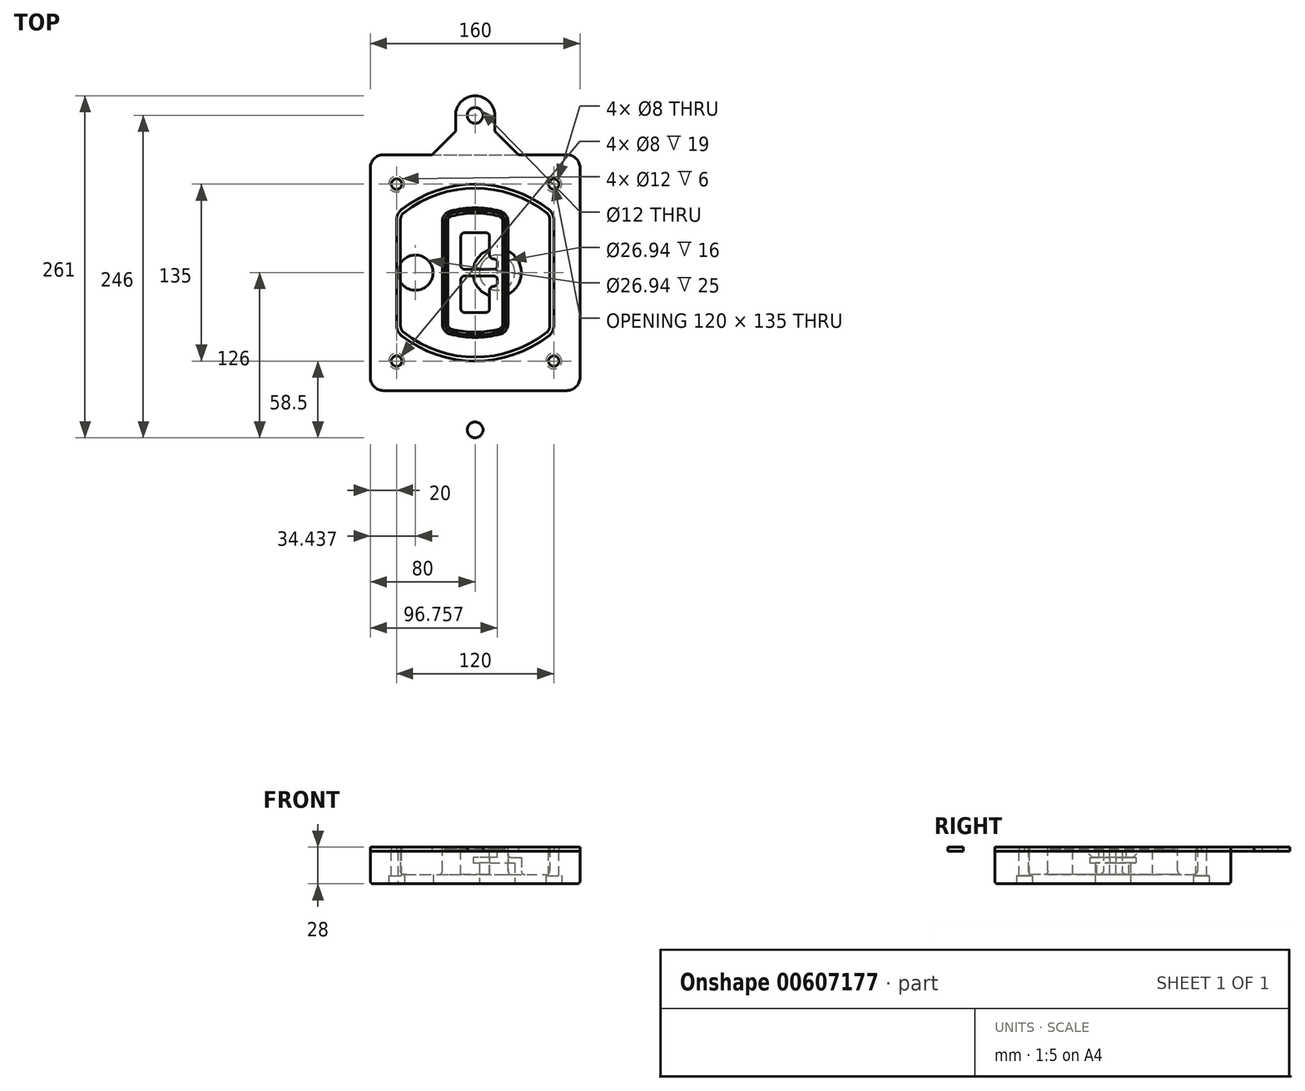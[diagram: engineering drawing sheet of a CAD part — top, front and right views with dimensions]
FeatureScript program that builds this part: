
annotation { "Feature Type Name" : "Feature", "Feature Type Description" : "" }
export const myFeature = defineFeature(function(context is Context, id is Id, definition is map)
    precondition{}
    {
        {
            var Q0;
            Q0=qCreatedBy(makeId("Top.planeOp"),FACE);
            var sketch = newSketch(context, id + "F0", { "sketchPlane" : qUnion([Q0])});
            skPoint(sketch, "E0.rect.middle", {"position": v(0, 0) * mm});
            skLineSegment(sketch, "E1.bottom", {"start": v(-70, -90) * mm, "end": v(70, -90) * mm});
            skLineSegment(sketch, "E1.top", {"start": v(-70, 90) * mm, "end": v(70, 90) * mm});
            skLineSegment(sketch, "E1.left", {"start": v(-80, -80) * mm, "end": v(-80, 80) * mm});
            skLineSegment(sketch, "E1.right", {"start": v(80, -80) * mm, "end": v(80, 80) * mm});
            skLineSegment(sketch, "E2", {"start": v(-80, 90) * mm, "end": v(80, -90) * mm, "construction": true});
            skLineSegment(sketch, "E3", {"start": v(80, 90) * mm, "end": v(-80, -90) * mm, "construction": true});
            skCircle(sketch, "E4", {"center": v(-60, 67.5) * mm, "radius": 4 * mm});
            skCircle(sketch, "E5", {"center": v(60, 67.5) * mm, "radius": 4 * mm});
            skCircle(sketch, "E6", {"center": v(60, -67.5) * mm, "radius": 4 * mm});
            skCircle(sketch, "E7", {"center": v(-60, -67.5) * mm, "radius": 4 * mm});
            skLineSegment(sketch, "E8", {"start": v(-60, 67.5) * mm, "end": v(60, 67.5) * mm, "construction": true});
            skLineSegment(sketch, "E9", {"start": v(60, 67.5) * mm, "end": v(60, -67.5) * mm, "construction": true});
            skLineSegment(sketch, "E10", {"start": v(60, -67.5) * mm, "end": v(-60, -67.5) * mm, "construction": true});
            skLineSegment(sketch, "E11", {"start": v(-60, -67.5) * mm, "end": v(-60, 67.5) * mm, "construction": true});
            skLineSegment(sketch, "E12", {"start": v(-60, 40.3) * mm, "end": v(-60, -40.3) * mm});
            skLineSegment(sketch, "E13", {"start": v(60, 40.3) * mm, "end": v(60, -40.3) * mm});
            skArc(sketch, "E14", {"start": v(56.15, 48.18) * mm, "mid": v(0, 67.5) * mm, "end": v(-56.15, 48.18) * mm});
            skArc(sketch, "E15", {"start": v(-56.15, -48.18) * mm, "mid": v(0, -67.5) * mm, "end": v(56.15, -48.18) * mm});
            skLineSegment(sketch, "E16", {"start": v(-60, 0) * mm, "end": v(60, 0) * mm, "construction": true});
            skPoint(sketch, "E17.visualSharp", {"position": v(-60, -45) * mm});
            skArc(sketch, "E17.filletArc", {"start": v(-60, -40.3) * mm, "mid": v(-58.99, -44.68) * mm, "end": v(-56.15, -48.18) * mm});
            skPoint(sketch, "E18.visualSharp", {"position": v(-60, 45) * mm});
            skArc(sketch, "E18.filletArc", {"start": v(-56.15, 48.18) * mm, "mid": v(-58.99, 44.68) * mm, "end": v(-60, 40.3) * mm});
            skPoint(sketch, "E19.visualSharp", {"position": v(60, 45) * mm});
            skArc(sketch, "E19.filletArc", {"start": v(60, 40.3) * mm, "mid": v(58.99, 44.68) * mm, "end": v(56.15, 48.18) * mm});
            skPoint(sketch, "E20.visualSharp", {"position": v(60, -45) * mm});
            skArc(sketch, "E20.filletArc", {"start": v(56.15, -48.18) * mm, "mid": v(58.99, -44.68) * mm, "end": v(60, -40.3) * mm});
            skPoint(sketch, "E21.visualSharp", {"position": v(-80, 90) * mm});
            skArc(sketch, "E21.filletArc", {"start": v(-70, 90) * mm, "mid": v(-77.07, 87.07) * mm, "end": v(-80, 80) * mm});
            skPoint(sketch, "E22.visualSharp", {"position": v(80, 90) * mm});
            skArc(sketch, "E22.filletArc", {"start": v(80, 80) * mm, "mid": v(77.07, 87.07) * mm, "end": v(70, 90) * mm});
            skPoint(sketch, "E23.visualSharp", {"position": v(80, -90) * mm});
            skArc(sketch, "E23.filletArc", {"start": v(70, -90) * mm, "mid": v(77.07, -87.07) * mm, "end": v(80, -80) * mm});
            skPoint(sketch, "E24.visualSharp", {"position": v(-80, -90) * mm});
            skArc(sketch, "E24.filletArc", {"start": v(-80, -80) * mm, "mid": v(-77.07, -87.07) * mm, "end": v(-70, -90) * mm});
            skArc(sketch, "E25.0", {"start": v(57, 40.3) * mm, "mid": v(56.3, 43.36) * mm, "end": v(54.3, 45.81) * mm});
            skLineSegment(sketch, "E25.1", {"start": v(57, 40.3) * mm, "end": v(57, -40.3) * mm});
            skArc(sketch, "E25.2", {"start": v(54.3, -45.81) * mm, "mid": v(56.3, -43.36) * mm, "end": v(57, -40.3) * mm});
            skArc(sketch, "E25.3", {"start": v(-54.3, -45.81) * mm, "mid": v(0, -64.5) * mm, "end": v(54.3, -45.81) * mm});
            skArc(sketch, "E25.4", {"start": v(-57, -40.3) * mm, "mid": v(-56.3, -43.36) * mm, "end": v(-54.3, -45.81) * mm});
            skArc(sketch, "E25.5", {"start": v(54.3, 45.81) * mm, "mid": v(0, 64.5) * mm, "end": v(-54.3, 45.81) * mm});
            skLineSegment(sketch, "E25.6", {"start": v(-57, 40.3) * mm, "end": v(-57, -40.3) * mm});
            skArc(sketch, "E25.7", {"start": v(-54.3, 45.81) * mm, "mid": v(-56.3, 43.36) * mm, "end": v(-57, 40.3) * mm});
            skArc(sketch, "E26.0", {"start": v(-58.62, 51.33) * mm, "mid": v(-62.58, 46.43) * mm, "end": v(-64, 40.3) * mm});
            skArc(sketch, "E26.1", {"start": v(58.62, 51.33) * mm, "mid": v(0, 71.5) * mm, "end": v(-58.62, 51.33) * mm});
            skArc(sketch, "E26.2", {"start": v(64, 40.3) * mm, "mid": v(62.58, 46.43) * mm, "end": v(58.62, 51.33) * mm});
            skLineSegment(sketch, "E26.3", {"start": v(64, 40.3) * mm, "end": v(64, -40.3) * mm});
            skArc(sketch, "E26.4", {"start": v(58.62, -51.33) * mm, "mid": v(62.58, -46.43) * mm, "end": v(64, -40.3) * mm});
            skLineSegment(sketch, "E26.5", {"start": v(-64, 40.3) * mm, "end": v(-64, -40.3) * mm});
            skArc(sketch, "E26.6", {"start": v(-58.62, -51.33) * mm, "mid": v(0, -71.5) * mm, "end": v(58.62, -51.33) * mm});
            skArc(sketch, "E26.7", {"start": v(-64, -40.3) * mm, "mid": v(-62.58, -46.43) * mm, "end": v(-58.62, -51.33) * mm});
            skSolve(sketch);
        }
        {
            var Q0;
            Q0=makeQuery(id+"F0.imprint","IMPRINT",FACE,{"disambiguationData":[TD([[makeQuery(id+"F0.imprint","IMPRINT",EDGE,{"derivedFrom":sQuery(id+"F0.wireOp",EDGE,"E1.bottom")}),1.0]])]});
            var Q1;
            Q1=makeQuery(id+"F0.imprint","IMPRINT",FACE,{"disambiguationData":[TD([[makeQuery(id+"F0.imprint","IMPRINT",EDGE,{"derivedFrom":sQuery(id+"F0.wireOp",EDGE,"E12")}),1.0]])]});
            var Q2;
            Q2=makeQuery(id+"F0.imprint","IMPRINT",FACE,{"disambiguationData":[TD([[makeQuery(id+"F0.imprint","IMPRINT",EDGE,{"derivedFrom":sQuery(id+"F0.wireOp",EDGE,"E25.0")}),1.0]])]});
            var Q3;
            Q3=makeQuery(id+"F0.imprint","IMPRINT",FACE,{"disambiguationData":[TD([[makeQuery(id+"F0.imprint","IMPRINT",EDGE,{"derivedFrom":sQuery(id+"F0.wireOp",EDGE,"E12")}),-1.0]])]});
            extrude(context, id + "F1", {"entities" : qUnion([Q0, Q1, Q2, Q3]), "oppositeDirection" : true, "depth" : 25 * mm});
        }
        {
            var Q0;
            Q0=makeQuery(id+"F0.imprint","IMPRINT",FACE,{"disambiguationData":[TD([[makeQuery(id+"F0.imprint","IMPRINT",EDGE,{"derivedFrom":sQuery(id+"F0.wireOp",EDGE,"E12")}),1.0]])]});
            extrude(context, id + "F2", {"entities" : qUnion([Q0]), "operationType" : NewBodyOperationType.ADD, "depth" : 3 * mm});
        }
        {
            var Q0;
            Q0=makeQuery(id+"F0.imprint","IMPRINT",FACE,{"disambiguationData":[TD([[makeQuery(id+"F0.imprint","IMPRINT",EDGE,{"derivedFrom":sQuery(id+"F0.wireOp",EDGE,"E25.0")}),1.0]])]});
            extrude(context, id + "F3", {"entities" : qUnion([Q0]), "operationType" : NewBodyOperationType.REMOVE, "oppositeDirection" : true, "depth" : 18 * mm});
        }
        {
            var Q0;
            Q0=makeQuery(id+"F2.opExtrude","CAP_FACE",FACE,{"disambiguationData":[OSD([sQuery(id+"F0.wireOp",EDGE,"E12"),sQuery(id+"F0.wireOp",EDGE,"E13"),sQuery(id+"F0.wireOp",EDGE,"E14"),sQuery(id+"F0.wireOp",EDGE,"E15"),sQuery(id+"F0.wireOp",EDGE,"E17.filletArc"),sQuery(id+"F0.wireOp",EDGE,"E18.filletArc"),sQuery(id+"F0.wireOp",EDGE,"E19.filletArc"),sQuery(id+"F0.wireOp",EDGE,"E20.filletArc"),sQuery(id+"F0.wireOp",EDGE,"E25.0"),sQuery(id+"F0.wireOp",EDGE,"E25.1"),sQuery(id+"F0.wireOp",EDGE,"E25.2"),sQuery(id+"F0.wireOp",EDGE,"E25.3"),sQuery(id+"F0.wireOp",EDGE,"E25.4"),sQuery(id+"F0.wireOp",EDGE,"E25.5"),sQuery(id+"F0.wireOp",EDGE,"E25.6"),sQuery(id+"F0.wireOp",EDGE,"E25.7")])],"isStart":false});
            var sketch = newSketch(context, id + "F4", { "sketchPlane" : qUnion([Q0])});
            skArc(sketch, "E27.0", {"start": v(-19.08, -46.97) * mm, "mid": v(0, -49.5) * mm, "end": v(19.08, -46.97) * mm});
            skArc(sketch, "E28.0", {"start": v(19.08, 46.97) * mm, "mid": v(0, 49.5) * mm, "end": v(-19.08, 46.97) * mm});
            skLineSegment(sketch, "E29", {"start": v(-25, 39.25) * mm, "end": v(-25, -39.25) * mm});
            skLineSegment(sketch, "E30", {"start": v(25, 39.25) * mm, "end": v(25, -39.25) * mm});
            skLineSegment(sketch, "E31", {"start": v(-25, 45.1) * mm, "end": v(25, 45.1) * mm, "construction": true});
            skLineSegment(sketch, "E32", {"start": v(-25, -45.1) * mm, "end": v(25, -45.1) * mm, "construction": true});
            skPoint(sketch, "E33.visualSharp", {"position": v(-25, 45.1) * mm});
            skArc(sketch, "E33.filletArc", {"start": v(-19.08, 46.97) * mm, "mid": v(-23.35, 44.11) * mm, "end": v(-25, 39.25) * mm});
            skPoint(sketch, "E34.visualSharp", {"position": v(25, 45.1) * mm});
            skArc(sketch, "E34.filletArc", {"start": v(25, 39.25) * mm, "mid": v(23.35, 44.11) * mm, "end": v(19.08, 46.97) * mm});
            skPoint(sketch, "E35.visualSharp", {"position": v(25, -45.1) * mm});
            skArc(sketch, "E35.filletArc", {"start": v(19.08, -46.97) * mm, "mid": v(23.35, -44.11) * mm, "end": v(25, -39.25) * mm});
            skPoint(sketch, "E36.visualSharp", {"position": v(-25, -45.1) * mm});
            skArc(sketch, "E36.filletArc", {"start": v(-25, -39.25) * mm, "mid": v(-23.35, -44.11) * mm, "end": v(-19.08, -46.97) * mm});
            skArc(sketch, "E37.0", {"start": v(54.3, 45.81) * mm, "mid": v(0, 64.5) * mm, "end": v(-54.3, 45.81) * mm});
            skArc(sketch, "E37.1", {"start": v(-54.3, 45.81) * mm, "mid": v(-56.3, 43.36) * mm, "end": v(-57, 40.3) * mm});
            skLineSegment(sketch, "E37.2", {"start": v(-57, 40.3) * mm, "end": v(-57, -40.3) * mm});
            skArc(sketch, "E37.3", {"start": v(-57, -40.3) * mm, "mid": v(-56.3, -43.36) * mm, "end": v(-54.3, -45.81) * mm});
            skArc(sketch, "E37.4", {"start": v(-54.3, -45.81) * mm, "mid": v(0, -64.5) * mm, "end": v(54.3, -45.81) * mm});
            skArc(sketch, "E37.5", {"start": v(54.3, -45.81) * mm, "mid": v(56.3, -43.36) * mm, "end": v(57, -40.3) * mm});
            skLineSegment(sketch, "E37.6", {"start": v(57, 40.3) * mm, "end": v(57, -40.3) * mm});
            skArc(sketch, "E37.7", {"start": v(57, 40.3) * mm, "mid": v(56.3, 43.36) * mm, "end": v(54.3, 45.81) * mm});
            skLineSegment(sketch, "E38.0", {"start": v(23, 39.25) * mm, "end": v(23, -39.25) * mm});
            skArc(sketch, "E38.1", {"start": v(18.56, -45.04) * mm, "mid": v(21.76, -42.9) * mm, "end": v(23, -39.25) * mm});
            skArc(sketch, "E38.2", {"start": v(-18.56, -45.04) * mm, "mid": v(0, -47.5) * mm, "end": v(18.56, -45.04) * mm});
            skArc(sketch, "E38.3", {"start": v(-23, -39.25) * mm, "mid": v(-21.76, -42.9) * mm, "end": v(-18.56, -45.04) * mm});
            skLineSegment(sketch, "E38.4", {"start": v(-23, 39.25) * mm, "end": v(-23, -39.25) * mm});
            skArc(sketch, "E38.5", {"start": v(23, 39.25) * mm, "mid": v(21.76, 42.9) * mm, "end": v(18.56, 45.04) * mm});
            skArc(sketch, "E38.6", {"start": v(-18.56, 45.04) * mm, "mid": v(-21.76, 42.9) * mm, "end": v(-23, 39.25) * mm});
            skArc(sketch, "E38.7", {"start": v(18.56, 45.04) * mm, "mid": v(0, 47.5) * mm, "end": v(-18.56, 45.04) * mm});
            skArc(sketch, "E39.0", {"start": v(21, 39.25) * mm, "mid": v(20.18, 41.68) * mm, "end": v(18.04, 43.1) * mm});
            skLineSegment(sketch, "E39.1", {"start": v(21, 39.25) * mm, "end": v(21, -39.25) * mm});
            skArc(sketch, "E39.2", {"start": v(18.04, -43.1) * mm, "mid": v(20.18, -41.68) * mm, "end": v(21, -39.25) * mm});
            skArc(sketch, "E39.3", {"start": v(-18.04, -43.1) * mm, "mid": v(0, -45.5) * mm, "end": v(18.04, -43.1) * mm});
            skArc(sketch, "E39.4", {"start": v(-21, -39.25) * mm, "mid": v(-20.18, -41.68) * mm, "end": v(-18.04, -43.1) * mm});
            skArc(sketch, "E39.5", {"start": v(18.04, 43.1) * mm, "mid": v(0, 45.5) * mm, "end": v(-18.04, 43.1) * mm});
            skLineSegment(sketch, "E39.6", {"start": v(-21, 39.25) * mm, "end": v(-21, -39.25) * mm});
            skArc(sketch, "E39.7", {"start": v(-18.04, 43.1) * mm, "mid": v(-20.18, 41.68) * mm, "end": v(-21, 39.25) * mm});
            skLineSegment(sketch, "E40", {"start": v(-25, 0) * mm, "end": v(25, 0) * mm, "construction": true});
            skLineSegment(sketch, "E41", {"start": v(-11, 5.5) * mm, "end": v(-11, 27.5) * mm});
            skLineSegment(sketch, "E42", {"start": v(-8, 30.5) * mm, "end": v(8, 30.5) * mm});
            skLineSegment(sketch, "E43", {"start": v(11, 27.5) * mm, "end": v(11, 13.5) * mm});
            skLineSegment(sketch, "E44", {"start": v(14, 10.5) * mm, "end": v(14, 10.5) * mm});
            skLineSegment(sketch, "E45", {"start": v(17, 7.5) * mm, "end": v(17, 5.5) * mm});
            skLineSegment(sketch, "E46", {"start": v(14, 2.5) * mm, "end": v(-8, 2.5) * mm});
            skPoint(sketch, "E47.visualSharp", {"position": v(-11, 30.5) * mm});
            skArc(sketch, "E47.filletArc", {"start": v(-8, 30.5) * mm, "mid": v(-10.12, 29.62) * mm, "end": v(-11, 27.5) * mm});
            skPoint(sketch, "E48.visualSharp", {"position": v(11, 30.5) * mm});
            skArc(sketch, "E48.filletArc", {"start": v(11, 27.5) * mm, "mid": v(10.12, 29.62) * mm, "end": v(8, 30.5) * mm});
            skPoint(sketch, "E49.visualSharp", {"position": v(11, 10.5) * mm});
            skArc(sketch, "E49.filletArc", {"start": v(11, 13.5) * mm, "mid": v(11.88, 11.38) * mm, "end": v(14, 10.5) * mm});
            skPoint(sketch, "E50.visualSharp", {"position": v(17, 10.5) * mm});
            skArc(sketch, "E50.filletArc", {"start": v(17, 7.5) * mm, "mid": v(16.12, 9.62) * mm, "end": v(14, 10.5) * mm});
            skPoint(sketch, "E51.visualSharp", {"position": v(17, 2.5) * mm});
            skArc(sketch, "E51.filletArc", {"start": v(14, 2.5) * mm, "mid": v(16.12, 3.38) * mm, "end": v(17, 5.5) * mm});
            skPoint(sketch, "E52.visualSharp", {"position": v(-11, 2.5) * mm});
            skArc(sketch, "E52.filletArc", {"start": v(-11, 5.5) * mm, "mid": v(-10.12, 3.38) * mm, "end": v(-8, 2.5) * mm});
            skLineSegment(sketch, "E53.0.MirrorCS", {"start": v(14, -2.5) * mm, "end": v(-8, -2.5) * mm});
            skArc(sketch, "E54.0.MirrorCS", {"start": v(-11, -5.5) * mm, "mid": v(-10.12, -3.38) * mm, "end": v(-8, -2.5) * mm});
            skLineSegment(sketch, "E55.0.MirrorCS", {"start": v(-11, -5.5) * mm, "end": v(-11, -27.5) * mm});
            skArc(sketch, "E56.0.MirrorCS", {"start": v(-8, -30.5) * mm, "mid": v(-10.12, -29.62) * mm, "end": v(-11, -27.5) * mm});
            skLineSegment(sketch, "E57.0.MirrorCS", {"start": v(-8, -30.5) * mm, "end": v(8, -30.5) * mm});
            skArc(sketch, "E58.0.MirrorCS", {"start": v(11, -27.5) * mm, "mid": v(10.12, -29.62) * mm, "end": v(8, -30.5) * mm});
            skLineSegment(sketch, "E59.0.MirrorCS", {"start": v(11, -27.5) * mm, "end": v(11, -13.5) * mm});
            skArc(sketch, "E60.0.MirrorCS", {"start": v(11, -13.5) * mm, "mid": v(11.88, -11.38) * mm, "end": v(14, -10.5) * mm});
            skArc(sketch, "E61.0.MirrorCS", {"start": v(17, -7.5) * mm, "mid": v(16.12, -9.62) * mm, "end": v(14, -10.5) * mm});
            skLineSegment(sketch, "E62.0.MirrorCS", {"start": v(17, -7.5) * mm, "end": v(17, -5.5) * mm});
            skArc(sketch, "E63.0.MirrorCS", {"start": v(14, -2.5) * mm, "mid": v(16.12, -3.38) * mm, "end": v(17, -5.5) * mm});
            skSolve(sketch);
        }
        {
            var Q0;
            Q0=makeQuery(id+"F4.imprint","IMPRINT",FACE,{"disambiguationData":[TD([[makeQuery(id+"F4.imprint","IMPRINT",EDGE,{"derivedFrom":sQuery(id+"F4.wireOp",EDGE,"E27.0")}),1.0]])]});
            var Q1;
            Q1=makeQuery(id+"F4.imprint","IMPRINT",FACE,{"disambiguationData":[TD([[makeQuery(id+"F4.imprint","IMPRINT",EDGE,{"derivedFrom":sQuery(id+"F4.wireOp",EDGE,"E38.0")}),-1.0]])]});
            var Q2;
            Q2=makeQuery(id+"F4.imprint","IMPRINT",FACE,{"disambiguationData":[TD([[makeQuery(id+"F4.imprint","IMPRINT",EDGE,{"derivedFrom":sQuery(id+"F4.wireOp",EDGE,"E39.0")}),1.0]])]});
            extrude(context, id + "F5", {"entities" : qUnion([Q0, Q1, Q2]), "operationType" : NewBodyOperationType.ADD, "endBound" : BoundingType.UP_TO_NEXT, "oppositeDirection" : true, "depth" : 25 * mm});
        }
        {
            var Q0;
            Q0=makeQuery(id+"F4.imprint","IMPRINT",FACE,{"disambiguationData":[TD([[makeQuery(id+"F4.imprint","IMPRINT",EDGE,{"derivedFrom":sQuery(id+"F4.wireOp",EDGE,"E38.0")}),-1.0]])]});
            extrude(context, id + "F6", {"entities" : qUnion([Q0]), "operationType" : NewBodyOperationType.REMOVE, "oppositeDirection" : true, "depth" : 2 * mm});
        }
        {
            var Q0;
            Q0=makeQuery(id+"F1.opExtrude","CAP_FACE",FACE,{"disambiguationData":[OSD([sQuery(id+"F0.wireOp",EDGE,"E1.bottom"),sQuery(id+"F0.wireOp",EDGE,"E1.top"),sQuery(id+"F0.wireOp",EDGE,"E1.left"),sQuery(id+"F0.wireOp",EDGE,"E1.right"),sQuery(id+"F0.wireOp",EDGE,"E4"),sQuery(id+"F0.wireOp",EDGE,"E5"),sQuery(id+"F0.wireOp",EDGE,"E6"),sQuery(id+"F0.wireOp",EDGE,"E7"),sQuery(id+"F0.wireOp",EDGE,"E21.filletArc"),sQuery(id+"F0.wireOp",EDGE,"E22.filletArc"),sQuery(id+"F0.wireOp",EDGE,"E23.filletArc"),sQuery(id+"F0.wireOp",EDGE,"E24.filletArc")])],"isStart":false});
            var sketch = newSketch(context, id + "F7", { "sketchPlane" : qUnion([Q0])});
            skCircle(sketch, "E64", {"center": v(16.76, 0) * mm, "radius": 13.47 * mm});
            skCircle(sketch, "E65", {"center": v(-45.56, 0) * mm, "radius": 13.47 * mm});
            skLineSegment(sketch, "E66", {"start": v(80, 0) * mm, "end": v(-80, 0) * mm});
            skCircle(sketch, "E67", {"center": v(16.76, 0) * mm, "radius": 18.47 * mm});
            skCircle(sketch, "E68", {"center": v(60, -67.5) * mm, "radius": 6 * mm});
            skCircle(sketch, "E69", {"center": v(-60, -67.5) * mm, "radius": 6 * mm});
            skCircle(sketch, "E70", {"center": v(-60, 67.5) * mm, "radius": 6 * mm});
            skCircle(sketch, "E71", {"center": v(60, 67.5) * mm, "radius": 6 * mm});
            skSolve(sketch);
        }
        {
            var Q0;
            {var subQ1=sQuery(id+"F7.wireOp",EDGE,"E66");var subQ4=sQuery(id+"F7.wireOp",EDGE,"E64");var subQ6=makeQuery(id+"F7.imprint","INTERSECT",VERTEX,{"disambiguationData":[OD(0.0)],"derivedFrom":[subQ4,subQ1]});Q0=makeQuery(id+"F7.imprint","IMPRINT",FACE,{"disambiguationData":[TD([[makeQuery(id+"F7.imprint","IMPRINT",EDGE,{"disambiguationData":[TD([[subQ6,-1.0]])],"derivedFrom":subQ4}),-1.0]])]});}
            var Q1;
            {var subQ0=sQuery(id+"F7.wireOp",EDGE,"E66");var subQ1=sQuery(id+"F7.wireOp",EDGE,"E64");var subQ3=makeQuery(id+"F7.imprint","INTERSECT",VERTEX,{"disambiguationData":[OD(0.0)],"derivedFrom":[subQ1,subQ0]});Q1=makeQuery(id+"F7.imprint","IMPRINT",FACE,{"disambiguationData":[TD([[makeQuery(id+"F7.imprint","IMPRINT",EDGE,{"disambiguationData":[TD([[subQ3,-1.0]])],"derivedFrom":subQ1}),1.0]])]});}
            var Q2;
            {var subQ0=sQuery(id+"F7.wireOp",EDGE,"E66");var subQ1=sQuery(id+"F7.wireOp",EDGE,"E64");var subQ3=makeQuery(id+"F7.imprint","INTERSECT",VERTEX,{"disambiguationData":[OD(0.0)],"derivedFrom":[subQ1,subQ0]});Q2=makeQuery(id+"F7.imprint","IMPRINT",FACE,{"disambiguationData":[TD([[makeQuery(id+"F7.imprint","IMPRINT",EDGE,{"disambiguationData":[TD([[subQ3,1.0]])],"derivedFrom":subQ1}),1.0]])]});}
            var Q3;
            {var subQ1=sQuery(id+"F7.wireOp",EDGE,"E66");var subQ4=sQuery(id+"F7.wireOp",EDGE,"E64");var subQ6=makeQuery(id+"F7.imprint","INTERSECT",VERTEX,{"disambiguationData":[OD(0.0)],"derivedFrom":[subQ4,subQ1]});Q3=makeQuery(id+"F7.imprint","IMPRINT",FACE,{"disambiguationData":[TD([[makeQuery(id+"F7.imprint","IMPRINT",EDGE,{"disambiguationData":[TD([[subQ6,1.0]])],"derivedFrom":subQ4}),-1.0]])]});}
            extrude(context, id + "F8", {"entities" : qUnion([Q0, Q1, Q2, Q3]), "operationType" : NewBodyOperationType.ADD, "oppositeDirection" : true, "depth" : 20 * mm});
        }
        {
            var Q0;
            {var subQ0=sQuery(id+"F7.wireOp",EDGE,"E66");var subQ1=sQuery(id+"F7.wireOp",EDGE,"E64");var subQ3=makeQuery(id+"F7.imprint","INTERSECT",VERTEX,{"disambiguationData":[OD(0.0)],"derivedFrom":[subQ1,subQ0]});Q0=makeQuery(id+"F7.imprint","IMPRINT",FACE,{"disambiguationData":[TD([[makeQuery(id+"F7.imprint","IMPRINT",EDGE,{"disambiguationData":[TD([[subQ3,-1.0]])],"derivedFrom":subQ1}),1.0]])]});}
            var Q1;
            {var subQ0=sQuery(id+"F7.wireOp",EDGE,"E66");var subQ1=sQuery(id+"F7.wireOp",EDGE,"E64");var subQ3=makeQuery(id+"F7.imprint","INTERSECT",VERTEX,{"disambiguationData":[OD(0.0)],"derivedFrom":[subQ1,subQ0]});Q1=makeQuery(id+"F7.imprint","IMPRINT",FACE,{"disambiguationData":[TD([[makeQuery(id+"F7.imprint","IMPRINT",EDGE,{"disambiguationData":[TD([[subQ3,1.0]])],"derivedFrom":subQ1}),1.0]])]});}
            extrude(context, id + "F9", {"entities" : qUnion([Q0, Q1]), "operationType" : NewBodyOperationType.REMOVE, "oppositeDirection" : true, "depth" : 16 * mm});
        }
        {
            var Q0;
            {var subQ0=sQuery(id+"F7.wireOp",EDGE,"E66");var subQ1=sQuery(id+"F7.wireOp",EDGE,"E65");var subQ3=makeQuery(id+"F7.imprint","INTERSECT",VERTEX,{"disambiguationData":[OD(0.0)],"derivedFrom":[subQ1,subQ0]});Q0=makeQuery(id+"F7.imprint","IMPRINT",FACE,{"disambiguationData":[TD([[makeQuery(id+"F7.imprint","IMPRINT",EDGE,{"disambiguationData":[TD([[subQ3,-1.0]])],"derivedFrom":subQ1}),1.0]])]});}
            var Q1;
            {var subQ0=sQuery(id+"F7.wireOp",EDGE,"E66");var subQ1=sQuery(id+"F7.wireOp",EDGE,"E65");var subQ3=makeQuery(id+"F7.imprint","INTERSECT",VERTEX,{"disambiguationData":[OD(0.0)],"derivedFrom":[subQ1,subQ0]});Q1=makeQuery(id+"F7.imprint","IMPRINT",FACE,{"disambiguationData":[TD([[makeQuery(id+"F7.imprint","IMPRINT",EDGE,{"disambiguationData":[TD([[subQ3,1.0]])],"derivedFrom":subQ1}),1.0]])]});}
            extrude(context, id + "F10", {"entities" : qUnion([Q0, Q1]), "operationType" : NewBodyOperationType.REMOVE, "oppositeDirection" : true, "depth" : 25 * mm});
        }
        {
            var Q0;
            Q0=makeQuery(id+"F7.imprint","IMPRINT",FACE,{"disambiguationData":[TD([[makeQuery(id+"F7.imprint","IMPRINT",EDGE,{"derivedFrom":sQuery(id+"F7.wireOp",EDGE,"E68")}),1.0]])]});
            var Q1;
            Q1=makeQuery(id+"F7.imprint","IMPRINT",FACE,{"disambiguationData":[TD([[makeQuery(id+"F7.imprint","IMPRINT",EDGE,{"derivedFrom":makeQuery(id+"F1.opExtrude","CAP_EDGE",EDGE,{"disambiguationData":[OSD([sQuery(id+"F0.wireOp",EDGE,"E5")])],"isStart":false})}),-1.0]])]});
            var Q2;
            Q2=makeQuery(id+"F7.imprint","IMPRINT",FACE,{"disambiguationData":[TD([[makeQuery(id+"F7.imprint","IMPRINT",EDGE,{"derivedFrom":sQuery(id+"F7.wireOp",EDGE,"E69")}),1.0]])]});
            var Q3;
            Q3=makeQuery(id+"F7.imprint","IMPRINT",FACE,{"disambiguationData":[TD([[makeQuery(id+"F7.imprint","IMPRINT",EDGE,{"derivedFrom":makeQuery(id+"F1.opExtrude","CAP_EDGE",EDGE,{"disambiguationData":[OSD([sQuery(id+"F0.wireOp",EDGE,"E4")])],"isStart":false})}),-1.0]])]});
            var Q4;
            Q4=makeQuery(id+"F7.imprint","IMPRINT",FACE,{"disambiguationData":[TD([[makeQuery(id+"F7.imprint","IMPRINT",EDGE,{"derivedFrom":sQuery(id+"F7.wireOp",EDGE,"E70")}),1.0]])]});
            var Q5;
            Q5=makeQuery(id+"F7.imprint","IMPRINT",FACE,{"disambiguationData":[TD([[makeQuery(id+"F7.imprint","IMPRINT",EDGE,{"derivedFrom":makeQuery(id+"F1.opExtrude","CAP_EDGE",EDGE,{"disambiguationData":[OSD([sQuery(id+"F0.wireOp",EDGE,"E7")])],"isStart":false})}),-1.0]])]});
            var Q6;
            Q6=makeQuery(id+"F7.imprint","IMPRINT",FACE,{"disambiguationData":[TD([[makeQuery(id+"F7.imprint","IMPRINT",EDGE,{"derivedFrom":sQuery(id+"F7.wireOp",EDGE,"E71")}),1.0]])]});
            var Q7;
            Q7=makeQuery(id+"F7.imprint","IMPRINT",FACE,{"disambiguationData":[TD([[makeQuery(id+"F7.imprint","IMPRINT",EDGE,{"derivedFrom":makeQuery(id+"F1.opExtrude","CAP_EDGE",EDGE,{"disambiguationData":[OSD([sQuery(id+"F0.wireOp",EDGE,"E6")])],"isStart":false})}),-1.0]])]});
            extrude(context, id + "F11", {"entities" : qUnion([Q0, Q1, Q2, Q3, Q4, Q5, Q6, Q7]), "operationType" : NewBodyOperationType.REMOVE, "oppositeDirection" : true, "depth" : 6 * mm});
        }
        {
            var Q0;
            Q0=makeQuery(id+"F9.boolean.opBoolean","COPY",FACE,{"derivedFrom":makeQuery(id+"F9.opExtrude","CAP_FACE",FACE,{"disambiguationData":[OSD([sQuery(id+"F7.wireOp",EDGE,"E64")])],"isStart":false})});
            var sketch = newSketch(context, id + "F12", { "sketchPlane" : qUnion([Q0])});
            skArc(sketch, "E72.0", {"start": v(11, 17.55) * mm, "mid": v(2.57, 11.82) * mm, "end": v(-1.54, 2.5) * mm});
            skArc(sketch, "E72.1", {"start": v(-1.54, -2.5) * mm, "mid": v(2.57, -11.82) * mm, "end": v(11, -17.55) * mm});
            skLineSegment(sketch, "E73", {"start": v(-1.54, -2.5) * mm, "end": v(14, -2.5) * mm});
            skLineSegment(sketch, "E74.0", {"start": v(14, 2.5) * mm, "end": v(-1.54, 2.5) * mm});
            skArc(sketch, "E74.1", {"start": v(14, 2.5) * mm, "mid": v(16.12, 3.38) * mm, "end": v(17, 5.5) * mm});
            skLineSegment(sketch, "E74.2", {"start": v(17, 7.5) * mm, "end": v(17, 5.5) * mm});
            skArc(sketch, "E74.3", {"start": v(17, 7.5) * mm, "mid": v(16.12, 9.62) * mm, "end": v(14, 10.5) * mm});
            skArc(sketch, "E74.4", {"start": v(11, 13.5) * mm, "mid": v(11.88, 11.38) * mm, "end": v(14, 10.5) * mm});
            skLineSegment(sketch, "E74.5", {"start": v(11, 17.55) * mm, "end": v(11, 13.5) * mm});
            skLineSegment(sketch, "E74.7", {"start": v(14, -2.5) * mm, "end": v(-1.54, -2.5) * mm});
            skArc(sketch, "E74.8", {"start": v(14, -2.5) * mm, "mid": v(16.12, -3.38) * mm, "end": v(17, -5.5) * mm});
            skLineSegment(sketch, "E74.9", {"start": v(17, -7.5) * mm, "end": v(17, -5.5) * mm});
            skArc(sketch, "E74.10", {"start": v(17, -7.5) * mm, "mid": v(16.12, -9.62) * mm, "end": v(14, -10.5) * mm});
            skArc(sketch, "E74.11", {"start": v(11, -13.5) * mm, "mid": v(11.88, -11.38) * mm, "end": v(14, -10.5) * mm});
            skLineSegment(sketch, "E74.12", {"start": v(11, -17.55) * mm, "end": v(11, -13.5) * mm});
            skPoint(sketch, "E75.orphan", {"position": v(11, -27.5) * mm});
            skPoint(sketch, "E76.orphan", {"position": v(-8, -2.5) * mm});
            skPoint(sketch, "E77.orphan", {"position": v(-8, 2.5) * mm});
            skPoint(sketch, "E78.orphan", {"position": v(11, 27.5) * mm});
            skSolve(sketch);
        }
        {
            var Q0;
            {var subQ7=sQuery(id+"F12.wireOp",EDGE,"E72.0");var subQ14=sQuery(id+"F12.wireOp",EDGE,"E72.1");var subQ16=sQuery(id+"F12.wireOp",EDGE,"E74.1");var subQ18=sQuery(id+"F12.wireOp",EDGE,"E74.8");Q0=qUnion([makeQuery(id+"F12.imprint","IMPRINT",FACE,{"disambiguationData":[TD([[makeQuery(id+"F12.imprint","IMPRINT",EDGE,{"derivedFrom":subQ7}),1.0]])]}),makeQuery(id+"F12.imprint","IMPRINT",FACE,{"disambiguationData":[TD([[makeQuery(id+"F12.imprint","IMPRINT",EDGE,{"derivedFrom":subQ14}),1.0]])]}),makeQuery(id+"F12.imprint","IMPRINT",FACE,{"disambiguationData":[TD([[makeQuery(id+"F12.imprint","IMPRINT",EDGE,{"derivedFrom":subQ16}),1.0]])]}),makeQuery(id+"F12.imprint","IMPRINT",FACE,{"disambiguationData":[TD([[makeQuery(id+"F12.imprint","IMPRINT",EDGE,{"derivedFrom":subQ18}),-1.0]])]})]);}
            var Q1;
            Q1=makeQuery(id+"F5.boolean.opBoolean","SPLIT",FACE,{"disambiguationData":[TD([makeQuery(id+"F5.opExtrude","SWEPT_FACE",FACE,{"disambiguationData":[OSD([sQuery(id+"F4.wireOp",EDGE,"E41")])]})])],"derivedFrom":makeQuery(id+"F3.boolean.opBoolean","COPY",FACE,{"derivedFrom":makeQuery(id+"F3.opExtrude","CAP_FACE",FACE,{"disambiguationData":[OSD([sQuery(id+"F0.wireOp",EDGE,"E25.0"),sQuery(id+"F0.wireOp",EDGE,"E25.1"),sQuery(id+"F0.wireOp",EDGE,"E25.2"),sQuery(id+"F0.wireOp",EDGE,"E25.3"),sQuery(id+"F0.wireOp",EDGE,"E25.4"),sQuery(id+"F0.wireOp",EDGE,"E25.5"),sQuery(id+"F0.wireOp",EDGE,"E25.6"),sQuery(id+"F0.wireOp",EDGE,"E25.7")])],"isStart":false})})});
            extrude(context, id + "F13", {"entities" : qUnion([Q0]), "operationType" : NewBodyOperationType.REMOVE, "endBound" : BoundingType.UP_TO_SURFACE, "endBoundEntityFace" : qUnion([Q1]), "depth" : 25 * mm});
        }
        {
            var Q0;
            Q0=makeQuery(id+"F3.boolean.opBoolean","COPY",EDGE,{"derivedFrom":makeQuery(id+"F3.opExtrude","CAP_EDGE",EDGE,{"disambiguationData":[OSD([sQuery(id+"F0.wireOp",EDGE,"E25.6")])],"isStart":false})});
            var Q1;
            Q1=makeQuery(id+"F8.boolean.opBoolean","INTERSECT",EDGE,{"derivedFrom":[makeQuery(id+"F5.opExtrude","SWEPT_FACE",FACE,{"disambiguationData":[OSD([sQuery(id+"F4.wireOp",EDGE,"E30")])]}),makeQuery(id+"F8.opExtrude","CAP_FACE",FACE,{"disambiguationData":[OSD([sQuery(id+"F7.wireOp",EDGE,"E67")])],"isStart":false})]});
            var Q2;
            Q2=makeQuery(id+"F8.boolean.opBoolean","INTERSECT",EDGE,{"disambiguationData":[OD(1.0)],"derivedFrom":[makeQuery(id+"F5.opExtrude","SWEPT_FACE",FACE,{"disambiguationData":[OSD([sQuery(id+"F4.wireOp",EDGE,"E30")])]}),makeQuery(id+"F8.opExtrude","SWEPT_FACE",FACE,{"disambiguationData":[OSD([sQuery(id+"F7.wireOp",EDGE,"E67")])]})]});
            var Q3;
            {var subQ0=sQuery(id+"F4.wireOp",EDGE,"E30");Q3=makeQuery(id+"F8.boolean.opBoolean","SPLIT",EDGE,{"disambiguationData":[TD([makeQuery(id+"F5.opExtrude","SWEPT_FACE",FACE,{"disambiguationData":[OSD([sQuery(id+"F4.wireOp",EDGE,"E35.filletArc")])]})])],"derivedFrom":makeQuery(id+"F5.opExtrude","CAP_EDGE",EDGE,{"disambiguationData":[OSD([subQ0])],"isStart":false})});}
            var Q4;
            {var subQ0=sQuery(id+"F0.wireOp",EDGE,"E25.7");var subQ1=sQuery(id+"F0.wireOp",EDGE,"E25.1");var subQ2=sQuery(id+"F0.wireOp",EDGE,"E25.6");var subQ3=sQuery(id+"F0.wireOp",EDGE,"E25.5");var subQ4=sQuery(id+"F0.wireOp",EDGE,"E25.4");var subQ5=sQuery(id+"F0.wireOp",EDGE,"E25.0");var subQ6=sQuery(id+"F0.wireOp",EDGE,"E25.2");var subQ7=sQuery(id+"F0.wireOp",EDGE,"E25.3");Q4=makeQuery(id+"F8.boolean.opBoolean","INTERSECT",EDGE,{"derivedFrom":[makeQuery(id+"F5.boolean.opBoolean","SPLIT",FACE,{"disambiguationData":[TD([makeQuery(id+"F2.opExtrude","SWEPT_FACE",FACE,{"disambiguationData":[OSD([subQ5])]})])],"derivedFrom":makeQuery(id+"F3.boolean.opBoolean","COPY",FACE,{"derivedFrom":makeQuery(id+"F3.opExtrude","CAP_FACE",FACE,{"disambiguationData":[OSD([subQ5,subQ1,subQ6,subQ7,subQ4,subQ3,subQ2,subQ0])],"isStart":false})})}),makeQuery(id+"F8.opExtrude","SWEPT_FACE",FACE,{"disambiguationData":[OSD([sQuery(id+"F7.wireOp",EDGE,"E67")])]})]});}
            var Q5;
            Q5=makeQuery(id+"F8.boolean.opBoolean","INTERSECT",EDGE,{"disambiguationData":[OD(0.0)],"derivedFrom":[makeQuery(id+"F5.opExtrude","SWEPT_FACE",FACE,{"disambiguationData":[OSD([sQuery(id+"F4.wireOp",EDGE,"E30")])]}),makeQuery(id+"F8.opExtrude","SWEPT_FACE",FACE,{"disambiguationData":[OSD([sQuery(id+"F7.wireOp",EDGE,"E67")])]})]});
            fillet(context, id + "F14", {"entities" : qUnion([Q0, Q1, Q2, Q3, Q4, Q5]), "radius" : 3 * mm, "tangentPropagation" : true, "allowEdgeOverflow" : false});
        }
        {
            var Q0;
            Q0=makeQuery(id+"F1.opExtrude","CAP_EDGE",EDGE,{"disambiguationData":[OSD([sQuery(id+"F0.wireOp",EDGE,"E1.bottom")])],"isStart":false});
            fillet(context, id + "F15", {"entities" : qUnion([Q0]), "radius" : 2 * mm, "tangentPropagation" : true, "allowEdgeOverflow" : false});
        }
        {
            var Q0;
            {var subQ0=sQuery(id+"F0.wireOp",EDGE,"E21.filletArc");var subQ1=sQuery(id+"F0.wireOp",EDGE,"E7");var subQ2=sQuery(id+"F0.wireOp",EDGE,"E6");var subQ3=sQuery(id+"F0.wireOp",EDGE,"E5");var subQ4=sQuery(id+"F0.wireOp",EDGE,"E4");var subQ5=sQuery(id+"F0.wireOp",EDGE,"E22.filletArc");var subQ6=sQuery(id+"F0.wireOp",EDGE,"E1.bottom");var subQ7=sQuery(id+"F0.wireOp",EDGE,"E1.right");var subQ8=sQuery(id+"F0.wireOp",EDGE,"E1.top");var subQ9=sQuery(id+"F0.wireOp",EDGE,"E1.left");var subQ10=sQuery(id+"F0.wireOp",EDGE,"E23.filletArc");var subQ11=sQuery(id+"F0.wireOp",EDGE,"E24.filletArc");Q0=makeQuery(id+"F2.boolean.opBoolean","SPLIT",FACE,{"disambiguationData":[TD([makeQuery(id+"F1.opExtrude","SWEPT_FACE",FACE,{"disambiguationData":[OSD([subQ6])]})])],"derivedFrom":makeQuery(id+"F1.opExtrude","CAP_FACE",FACE,{"disambiguationData":[OSD([subQ6,subQ8,subQ9,subQ7,subQ4,subQ3,subQ2,subQ1,subQ0,subQ5,subQ10,subQ11])],"isStart":true})});}
            var sketch = newSketch(context, id + "F16", { "sketchPlane" : qUnion([Q0])});
            skSolve(sketch);
        }
        {
            var Q0;
            Q0=makeQuery(id+"F16.imprint","IMPRINT",FACE,{"disambiguationData":[TD([[makeQuery(id+"F16.imprint","IMPRINT",EDGE,{"derivedFrom":makeQuery(id+"F1.opExtrude","CAP_EDGE",EDGE,{"disambiguationData":[OSD([sQuery(id+"F0.wireOp",EDGE,"E1.bottom")])],"isStart":true})}),1.0]])]});
            var sketch = newSketch(context, id + "F17", { "sketchPlane" : qUnion([Q0])});
            skCircle(sketch, "E79", {"center": v(0, 120) * mm, "radius": 6 * mm});
            skLineSegment(sketch, "E80", {"start": v(-33, 90) * mm, "end": v(-15, 108) * mm});
            skLineSegment(sketch, "E81", {"start": v(-15, 108) * mm, "end": v(-15, 120) * mm});
            skLineSegment(sketch, "E82", {"start": v(33, 90) * mm, "end": v(15, 108) * mm});
            skLineSegment(sketch, "E83", {"start": v(15, 108) * mm, "end": v(15, 120) * mm});
            skArc(sketch, "E84", {"start": v(15, 120) * mm, "mid": v(0, 135) * mm, "end": v(-15, 120) * mm});
            skLineSegment(sketch, "E85", {"start": v(0, 120) * mm, "end": v(0, 90) * mm, "construction": true});
            skLineSegment(sketch, "E86", {"start": v(-80, 0) * mm, "end": v(80, 0) * mm, "construction": true});
            skLineSegment(sketch, "E87", {"start": v(-33, 90) * mm, "end": v(33, 90) * mm});
            skCircle(sketch, "E88.MirrorC", {"center": v(0, -120) * mm, "radius": 6 * mm});
            skLineSegment(sketch, "E89.MirrorCS", {"start": v(-33, -90) * mm, "end": v(-15, -108) * mm});
            skLineSegment(sketch, "E90.MirrorCS", {"start": v(-15, -108) * mm, "end": v(-15, -120) * mm});
            skLineSegment(sketch, "E91.MirrorCS", {"start": v(33, -90) * mm, "end": v(15, -108) * mm});
            skLineSegment(sketch, "E92.MirrorCS", {"start": v(15, -108) * mm, "end": v(15, -120) * mm});
            skArc(sketch, "E93.MirrorCS", {"start": v(15, -120) * mm, "mid": v(0, -135) * mm, "end": v(-15, -120) * mm});
            skLineSegment(sketch, "E94.MirrorCS", {"start": v(0, -120) * mm, "end": v(0, -90) * mm, "construction": true});
            skLineSegment(sketch, "E95.MirrorCS", {"start": v(-33, -90) * mm, "end": v(33, -90) * mm});
            skLineSegment(sketch, "E96.0.0", {"start": v(70, 90) * mm, "end": v(-70, 90) * mm});
            skArc(sketch, "E96.0.1", {"start": v(-70, 90) * mm, "mid": v(-77.07, 87.07) * mm, "end": v(-80, 80) * mm});
            skLineSegment(sketch, "E96.0.2", {"start": v(-80, 80) * mm, "end": v(-80, -80) * mm});
            skArc(sketch, "E96.0.3", {"start": v(-80, -80) * mm, "mid": v(-77.07, -87.07) * mm, "end": v(-70, -90) * mm});
            skLineSegment(sketch, "E96.0.4", {"start": v(-70, -90) * mm, "end": v(70, -90) * mm});
            skArc(sketch, "E96.0.5", {"start": v(70, -90) * mm, "mid": v(77.07, -87.07) * mm, "end": v(80, -80) * mm});
            skLineSegment(sketch, "E96.0.6", {"start": v(80, -80) * mm, "end": v(80, 80) * mm});
            skArc(sketch, "E96.0.7", {"start": v(80, 80) * mm, "mid": v(77.07, 87.07) * mm, "end": v(70, 90) * mm});
            skSolve(sketch);
        }
        {
            var Q0;
            {var subQ1=sQuery(id+"F17.wireOp",EDGE,"E96.0.1");Q0=makeQuery(id+"F17.imprint","IMPRINT",FACE,{"disambiguationData":[TD([[makeQuery(id+"F17.imprint","IMPRINT",EDGE,{"derivedFrom":subQ1}),1.0]])]});}
            var Q1;
            Q1=makeQuery(id+"F17.imprint","IMPRINT",FACE,{"disambiguationData":[TD([[makeQuery(id+"F17.imprint","IMPRINT",EDGE,{"derivedFrom":sQuery(id+"F17.wireOp",EDGE,"E79")}),-1.0]])]});
            var Q2;
            Q2=makeQuery(id+"F17.imprint","IMPRINT",FACE,{"disambiguationData":[TD([[makeQuery(id+"F17.imprint","IMPRINT",EDGE,{"derivedFrom":sQuery(id+"F17.wireOp",EDGE,"E88.MirrorC")}),1.0]])]});
            var Q3;
            Q3=makeQuery(id+"F2.opExtrude","CAP_FACE",FACE,{"disambiguationData":[OSD([sQuery(id+"F0.wireOp",EDGE,"E12"),sQuery(id+"F0.wireOp",EDGE,"E13"),sQuery(id+"F0.wireOp",EDGE,"E14"),sQuery(id+"F0.wireOp",EDGE,"E15"),sQuery(id+"F0.wireOp",EDGE,"E17.filletArc"),sQuery(id+"F0.wireOp",EDGE,"E18.filletArc"),sQuery(id+"F0.wireOp",EDGE,"E19.filletArc"),sQuery(id+"F0.wireOp",EDGE,"E20.filletArc"),sQuery(id+"F0.wireOp",EDGE,"E25.0"),sQuery(id+"F0.wireOp",EDGE,"E25.1"),sQuery(id+"F0.wireOp",EDGE,"E25.2"),sQuery(id+"F0.wireOp",EDGE,"E25.3"),sQuery(id+"F0.wireOp",EDGE,"E25.4"),sQuery(id+"F0.wireOp",EDGE,"E25.5"),sQuery(id+"F0.wireOp",EDGE,"E25.6"),sQuery(id+"F0.wireOp",EDGE,"E25.7")])],"isStart":false});
            extrude(context, id + "F18", {"entities" : qUnion([Q0, Q1, Q2]), "endBound" : BoundingType.UP_TO_SURFACE, "depth" : 25 * mm, "endBoundEntityFace" : qUnion([Q3]), "offsetDistance" : 25 * mm});
        }
    });
